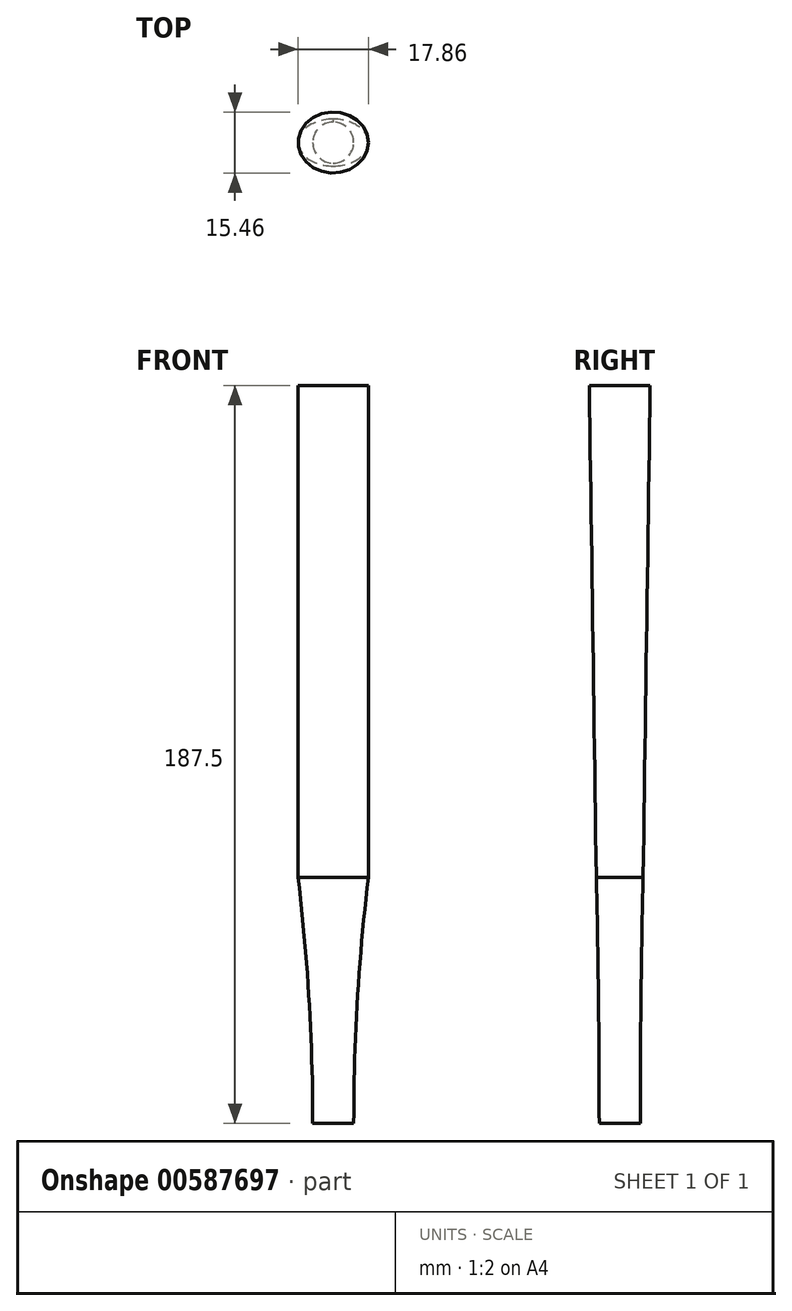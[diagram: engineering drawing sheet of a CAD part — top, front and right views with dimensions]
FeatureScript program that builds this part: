
annotation { "Feature Type Name" : "Feature", "Feature Type Description" : "" }
export const myFeature = defineFeature(function(context is Context, id is Id, definition is map)
    precondition{}
    {
        {
            var Q0;
            Q0=qCreatedBy(makeId("Front.planeOp"),FACE);
            var sketch = newSketch(context, id + "F0", { "sketchPlane" : qUnion([Q0])});
            skLineSegment(sketch, "E0", {"start": v(-3.8, 87.77) * mm, "end": v(-3.8, 275.27) * mm});
            skLineSegment(sketch, "E1", {"start": v(-12.74, 275.27) * mm, "end": v(5.12, 275.27) * mm});
            skLineSegment(sketch, "E2", {"start": v(-12.74, 150.27) * mm, "end": v(5.12, 150.27) * mm});
            skLineSegment(sketch, "E3", {"start": v(-9.02, 87.77) * mm, "end": v(1.4, 87.77) * mm});
            skArc(sketch, "E4", {"start": v(-9.02, 87.77) * mm, "mid": v(-9.95, 119.08) * mm, "end": v(-12.74, 150.27) * mm});
            skArc(sketch, "E5", {"start": v(1.4, 87.77) * mm, "mid": v(2.33, 119.08) * mm, "end": v(5.12, 150.27) * mm});
            skLineSegment(sketch, "E6.trimOffspring", {"start": v(5.12, 259.8) * mm, "end": v(5.12, 150.27) * mm});
            skLineSegment(sketch, "E7.trimOffspring", {"start": v(-12.74, 259.8) * mm, "end": v(-12.74, 150.27) * mm});
            skLineSegment(sketch, "E8", {"start": v(0.98, 275.27) * mm, "end": v(-0.5, 87.77) * mm});
            skLineSegment(sketch, "E9", {"start": v(-7.13, 87.77) * mm, "end": v(-8.6, 275.27) * mm});
            skLineSegment(sketch, "E10", {"start": v(-12.74, 259.8) * mm, "end": v(-12.74, 275.27) * mm});
            skLineSegment(sketch, "E11", {"start": v(5.12, 259.8) * mm, "end": v(5.12, 275.27) * mm});
            skLineSegment(sketch, "E12", {"start": v(-3.8, 270.49) * mm, "end": v(5.12, 270.49) * mm});
            skLineSegment(sketch, "E13", {"start": v(-3.8, 270.49) * mm, "end": v(-12.74, 270.49) * mm});
            skSolve(sketch);
        }
        {
            var Q0;
            Q0=qCreatedBy(makeId("Top.planeOp"),FACE);
            var Q1;
            Q1=sQuery(id+"F0.wireOp",VERTEX,"E0.end");
            cPlane(context, id + "F1", {"entities" : qUnion([Q0, Q1]), "cplaneType" : CPlaneType.PLANE_POINT, "offset" : 25 * mm, "width" : 150 * mm, "height" : 150 * mm});
        }
        {
            var Q0;
            Q0=qCreatedBy(id+"F1.planeOp",FACE);
            var sketch = newSketch(context, id + "F2", { "sketchPlane" : qUnion([Q0])});
            skPoint(sketch, "E14.0", {"position": v(-12.74, 0) * mm});
            skPoint(sketch, "E15.0", {"position": v(-8.6, 0) * mm});
            skPoint(sketch, "E16.0", {"position": v(-3.8, 0) * mm});
            skPoint(sketch, "E17.0", {"position": v(0.98, 0) * mm});
            skPoint(sketch, "E18.0", {"position": v(5.12, 0) * mm});
            skCircle(sketch, "E19.cCircle", {"center": v(-3.8, 0) * mm, "radius": 8.93 * mm, "construction": true});
            skLineSegment(sketch, "E19.0", {"start": v(5.12, 0) * mm, "end": v(0.65, -7.73) * mm, "construction": true});
            skLineSegment(sketch, "E19.1", {"start": v(0.65, -7.73) * mm, "end": v(-8.27, -7.73) * mm, "construction": true});
            skLineSegment(sketch, "E19.2", {"start": v(-8.27, -7.73) * mm, "end": v(-12.74, 0) * mm, "construction": true});
            skLineSegment(sketch, "E19.3", {"start": v(-12.74, 0) * mm, "end": v(-8.27, 7.73) * mm, "construction": true});
            skLineSegment(sketch, "E19.4", {"start": v(-8.27, 7.73) * mm, "end": v(0.65, 7.73) * mm, "construction": true});
            skLineSegment(sketch, "E19.5", {"start": v(0.65, 7.73) * mm, "end": v(5.12, 0) * mm, "construction": true});
            skLineSegment(sketch, "E20", {"start": v(-8.27, -7.73) * mm, "end": v(-3.8, 8.93) * mm, "construction": true});
            skPoint(sketch, "E20.endSnap0", {"position": v(-3.8, 7.73) * mm});
            skLineSegment(sketch, "E21", {"start": v(-3.8, 8.93) * mm, "end": v(0.65, -7.73) * mm, "construction": true});
            skLineSegment(sketch, "E22", {"start": v(0.65, 7.73) * mm, "end": v(-3.8, -8.93) * mm, "construction": true});
            skPoint(sketch, "E22.endSnap0", {"position": v(-3.8, -7.73) * mm});
            skLineSegment(sketch, "E23", {"start": v(-3.8, -8.93) * mm, "end": v(-8.27, 7.73) * mm, "construction": true});
            skEllipse(sketch, "E24", {"center": v(-3.8, 0) * mm, "majorRadius": 8.93 * mm, "minorRadius": 7.73 * mm, "majorAxis": v(1, 0)});
            skSolve(sketch);
        }
        {
            var Q0;
            Q0=qCreatedBy(makeId("Top.planeOp"),FACE);
            var Q1;
            Q1=sQuery(id+"F0.wireOp",VERTEX,"E4.start");
            cPlane(context, id + "F3", {"entities" : qUnion([Q0, Q1]), "cplaneType" : CPlaneType.PLANE_POINT, "offset" : 25 * mm, "width" : 150 * mm, "height" : 150 * mm});
        }
        {
            var Q0;
            Q0=qCreatedBy(id+"F3.planeOp",FACE);
            var sketch = newSketch(context, id + "F4", { "sketchPlane" : qUnion([Q0])});
            skPoint(sketch, "E25.0", {"position": v(-9.02, 0) * mm});
            skPoint(sketch, "E26.0", {"position": v(1.4, 0) * mm});
            skPoint(sketch, "E27.0", {"position": v(-3.8, 0) * mm});
            skCircle(sketch, "E28", {"center": v(-3.8, 0) * mm, "radius": 5.2 * mm});
            skSolve(sketch);
        }
        {
            var Q0;
            Q0=qCreatedBy(makeId("Top.planeOp"),FACE);
            var Q1;
            Q1=sQuery(id+"F0.wireOp",VERTEX,"E4.end");
            cPlane(context, id + "F5", {"entities" : qUnion([Q0, Q1]), "cplaneType" : CPlaneType.PLANE_POINT, "offset" : 25 * mm, "width" : 150 * mm, "height" : 150 * mm});
        }
        {
            var Q0;
            Q0=qCreatedBy(id+"F5.planeOp",FACE);
            var sketch = newSketch(context, id + "F6", { "sketchPlane" : qUnion([Q0])});
            skPoint(sketch, "E29.0", {"position": v(5.12, 0) * mm});
            skPoint(sketch, "E30.0", {"position": v(-12.74, 0) * mm});
            skPoint(sketch, "E31.0", {"position": v(-3.8, 0) * mm});
            skPoint(sketch, "E32.0", {"position": v(-3.8, 8.93) * mm});
            skLineSegment(sketch, "E33", {"start": v(-3.8, 8.93) * mm, "end": v(-3.8, 0) * mm, "construction": true});
            skCircle(sketch, "E34", {"center": v(-3.8, 2.98) * mm, "radius": 2.98 * mm, "construction": true});
            skCircle(sketch, "E35", {"center": v(-3.8, 5.95) * mm, "radius": 2.98 * mm, "construction": true});
            skEllipse(sketch, "E36", {"center": v(-3.8, 0) * mm, "majorRadius": 8.93 * mm, "minorRadius": 5.95 * mm, "majorAxis": v(1, 0)});
            skSolve(sketch);
        }
        {
            var Q0;
            Q0=makeQuery(id+"F2.imprint","IMPRINT",FACE,{"disambiguationData":[TD([[makeQuery(id+"F2.imprint","IMPRINT",EDGE,{"derivedFrom":sQuery(id+"F2.wireOp",EDGE,"E24")}),1.0]])]});
            var Q1;
            Q1=makeQuery(id+"F6.imprint","IMPRINT",FACE,{"disambiguationData":[TD([[makeQuery(id+"F6.imprint","IMPRINT",EDGE,{"derivedFrom":sQuery(id+"F6.wireOp",EDGE,"E36")}),1.0]])]});
            loft(context, id + "F7", {"sheetProfilesArray" : [{ "sheetProfileEntities" : qUnion([Q0]) }, { "sheetProfileEntities" : qUnion([Q1]) }]});
        }
        {
            var Q0;
            Q0=sQuery(id+"F0.wireOp",EDGE,"E2");
            cPoint(context, id + "F8", {"entities" : qUnion([Q0]), "parameter" : 0.5});
        }
        {
            var Q0;
            Q0=qCreatedBy(makeId("Right.planeOp"),FACE);
            var Q1;
            Q1 = qCreatedBy(id + "F8" ,VERTEX);
            cPlane(context, id + "F9", {"entities" : qUnion([Q0, Q1]), "cplaneType" : CPlaneType.PLANE_POINT, "offset" : 25 * mm, "width" : 150 * mm, "height" : 150 * mm});
        }
        {
            var Q0;
            Q0=qCreatedBy(id+"F9.planeOp",FACE);
            var sketch = newSketch(context, id + "F10", { "sketchPlane" : qUnion([Q0])});
            skPoint(sketch, "E37.0", {"position": v(0, 150.27) * mm});
            skFitSpline(sketch, "E38.0", {"points": [v(5.95, 150.27) * mm, v(1.98, 150.27) * mm, v(-1.98, 150.27) * mm, v(-5.95, 150.27) * mm]});
            skLineSegment(sketch, "E39.0", {"start": v(-5.2, 87.77) * mm, "end": v(5.2, 87.77) * mm});
            skLineSegment(sketch, "E40", {"start": v(-5.2, 87.77) * mm, "end": v(-5.2, 83.54) * mm, "construction": true});
            skLineSegment(sketch, "E41", {"start": v(5.2, 87.77) * mm, "end": v(5.2, 83.73) * mm, "construction": true});
            skArc(sketch, "E42", {"start": v(-5.2, 87.77) * mm, "mid": v(-5.4, 119.02) * mm, "end": v(-5.95, 150.27) * mm});
            skArc(sketch, "E43", {"start": v(5.2, 87.77) * mm, "mid": v(5.4, 119.02) * mm, "end": v(5.95, 150.27) * mm});
            skSolve(sketch);
        }
        {
            var Q1;
            Q1=makeQuery(id+"F7.opLoft","CAP_FACE",FACE,{"disambiguationData":[OSD([makeQuery(id+"F6.imprint","IMPRINT",FACE,{"disambiguationData":[TD([[makeQuery(id+"F6.imprint","IMPRINT",EDGE,{"derivedFrom":sQuery(id+"F6.wireOp",EDGE,"E36")}),1.0]])]})])],"isStart":true});
            var Q2;
            Q2=makeQuery(id+"F4.imprint","IMPRINT",FACE,{"disambiguationData":[TD([[makeQuery(id+"F4.imprint","IMPRINT",EDGE,{"derivedFrom":sQuery(id+"F4.wireOp",EDGE,"E28")}),1.0]])]});
            var Q3;
            Q3=sQuery(id+"F0.wireOp",EDGE,"E5");
            var Q4;
            Q4=sQuery(id+"F0.wireOp",EDGE,"E4");
            var Q5;
            Q5=sQuery(id+"F10.wireOp",EDGE,"E42");
            var Q6;
            Q6=sQuery(id+"F10.wireOp",EDGE,"E43");
            loft(context, id + "F11", {"operationType" : NewBodyOperationType.ADD, "addGuides" : true, "sheetProfilesArray" : [{ "sheetProfileEntities" : qUnion([Q1]) }, { "sheetProfileEntities" : qUnion([Q2]) }], "guidesArray" : [{ "guideEntities" : qUnion([Q3]), "guideDerivativeType" : LoftGuideDerivativeType.DEFAULT, "guideDerivativeMagnitude" : 1 }, { "guideEntities" : qUnion([Q4]), "guideDerivativeType" : LoftGuideDerivativeType.DEFAULT, "guideDerivativeMagnitude" : 1 }, { "guideEntities" : qUnion([Q5]), "guideDerivativeType" : LoftGuideDerivativeType.DEFAULT, "guideDerivativeMagnitude" : 1 }, { "guideEntities" : qUnion([Q6]), "guideDerivativeType" : LoftGuideDerivativeType.DEFAULT, "guideDerivativeMagnitude" : 1 }]});
        }
    });
